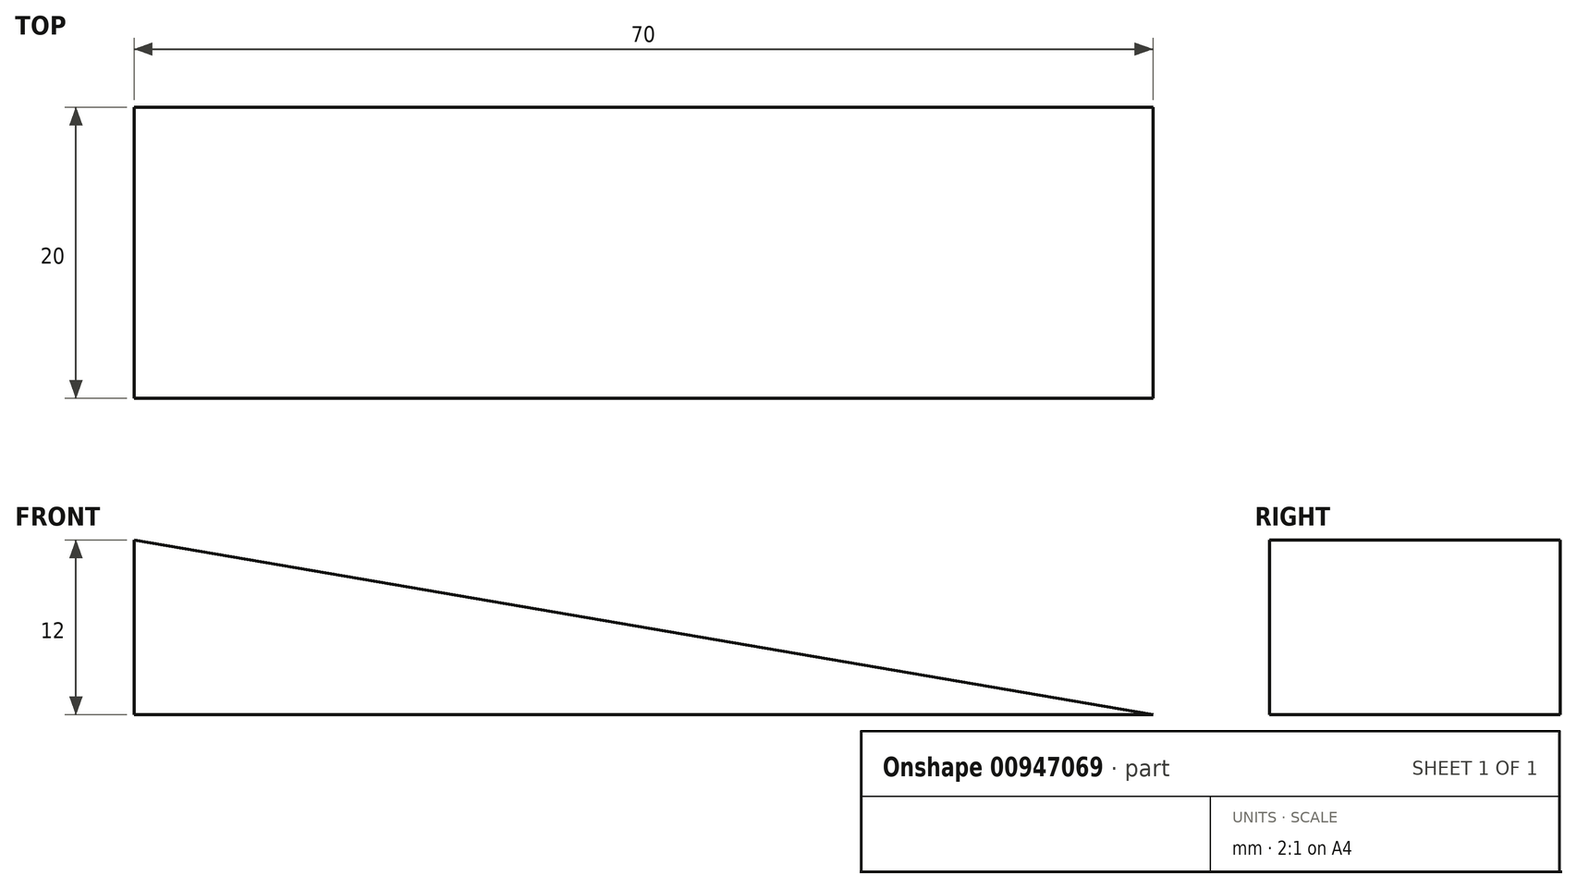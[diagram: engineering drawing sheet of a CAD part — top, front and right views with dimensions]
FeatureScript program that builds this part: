
annotation { "Feature Type Name" : "Feature", "Feature Type Description" : "" }
export const myFeature = defineFeature(function(context is Context, id is Id, definition is map)
    precondition{}
    {
        {
            var Q0;
            Q0=qCreatedBy(makeId("Front.planeOp"),FACE);
            var sketch = newSketch(context, id + "F0", { "sketchPlane" : qUnion([Q0])});
            skLineSegment(sketch, "E0", {"start": v(0, 0) * mm, "end": v(0, 12) * mm});
            skLineSegment(sketch, "E1", {"start": v(0, 12) * mm, "end": v(70, 0) * mm});
            skLineSegment(sketch, "E2", {"start": v(70, 0) * mm, "end": v(0, 0) * mm});
            skSolve(sketch);
        }
        {
            var Q0;
            Q0=makeQuery(id+"F0.imprint","IMPRINT",FACE,{"disambiguationData":[TD([[makeQuery(id+"F0.imprint","IMPRINT",EDGE,{"derivedFrom":sQuery(id+"F0.wireOp",EDGE,"E0")}),-1.0]])]});
            extrude(context, id + "F1", {"entities" : qUnion([Q0]), "depth" : 20 * mm, "offsetDistance" : 25 * mm});
        }
    });
